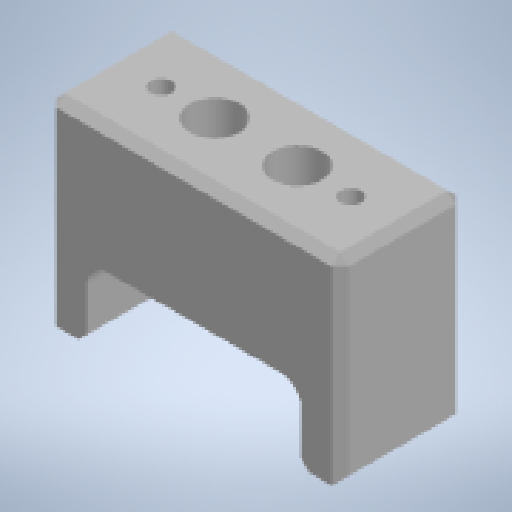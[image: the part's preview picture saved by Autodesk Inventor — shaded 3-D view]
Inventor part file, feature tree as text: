
AUTODESK INVENTOR PART (.ipt)
format: ipt  version: 2023 (Build 270158000, 158)  size: 257,024 bytes
history: native  units: in
note: dims shown in document units (in); Inventor stores cm internally (conversion verified against a paired STEP export)
features: extrude x7, sketch x5, plane x1, thicken_offset x1, chamfer x1
ambient origin geometry x8: Origin, YZ Plane, XZ Plane, XY Plane, X Axis, Y Axis, Z Axis, Center Point
bodies: Solid1 (feature_tree)
feature tree (15):
  sketch  "Sketch1"  dims[d0=0.7874in d1=2.3622in]
  extrude  "Extrusion1"  Depth=2.3622in
  extrude  "Extrusion3"  Depth=0.0197in
  extrude  "Extrusion4"  Depth=0.0197in
  plane  "Work Plane3"
  extrude  "Extrusion5"  Depth=1.811in
  extrude  "Extrusion2"  Depth=1.1811in
  extrude  "Extrusion8"  Depth=0.3937in TaperAngle=0.0deg
  thicken_offset  "Thicken1"
  extrude  "Extrusion11"  Depth=0.3937in TaperAngle=0.0deg
  chamfer  "Chamfer1"  Distance=1.7062in
  sketch  "Sketch2"  dims[d2=0.0197in d3=0.0197in]
  sketch  "Sketch3"  dims[d4=0.0197in d5=0.0197in]
  sketch  "Sketch8"  dims[d6=0.1969in d7=1.811in]
  sketch  "Sketch11"  dims[d9=2.7874in d10=1.1811in d11=1.1969in d12=0.0in d13=1.3937in d14=0.0in d15=1.7062in d16=0.1969in d17=0.0in d18=0.0in d19=1.7062in d20=1.1969in d21=0.0in d22=0.0in d27=0.3937in d28=0.0in d31=0.3937in d32=0.0in d44=1.3937in d64=0.0394in d65=0.1181in d66=135.0deg d67=0.0787in d69=0.1358in d71=0.689in d72=0.2819in d73=0.0935in d74=0.0525in d75=0.0953in d76=0.6063in d77=0.3937in d78=0.3937in d79=0.0in d80=0.0394in d81=0.0394in d82=0.2362in d94=2.0394in d95=0.689in d96=0.2in d98=0.7874in d99=0.4724in d100=0.3937in d101=0.0in d102=0.0787in d103=0.0787in d104=45.0deg]
